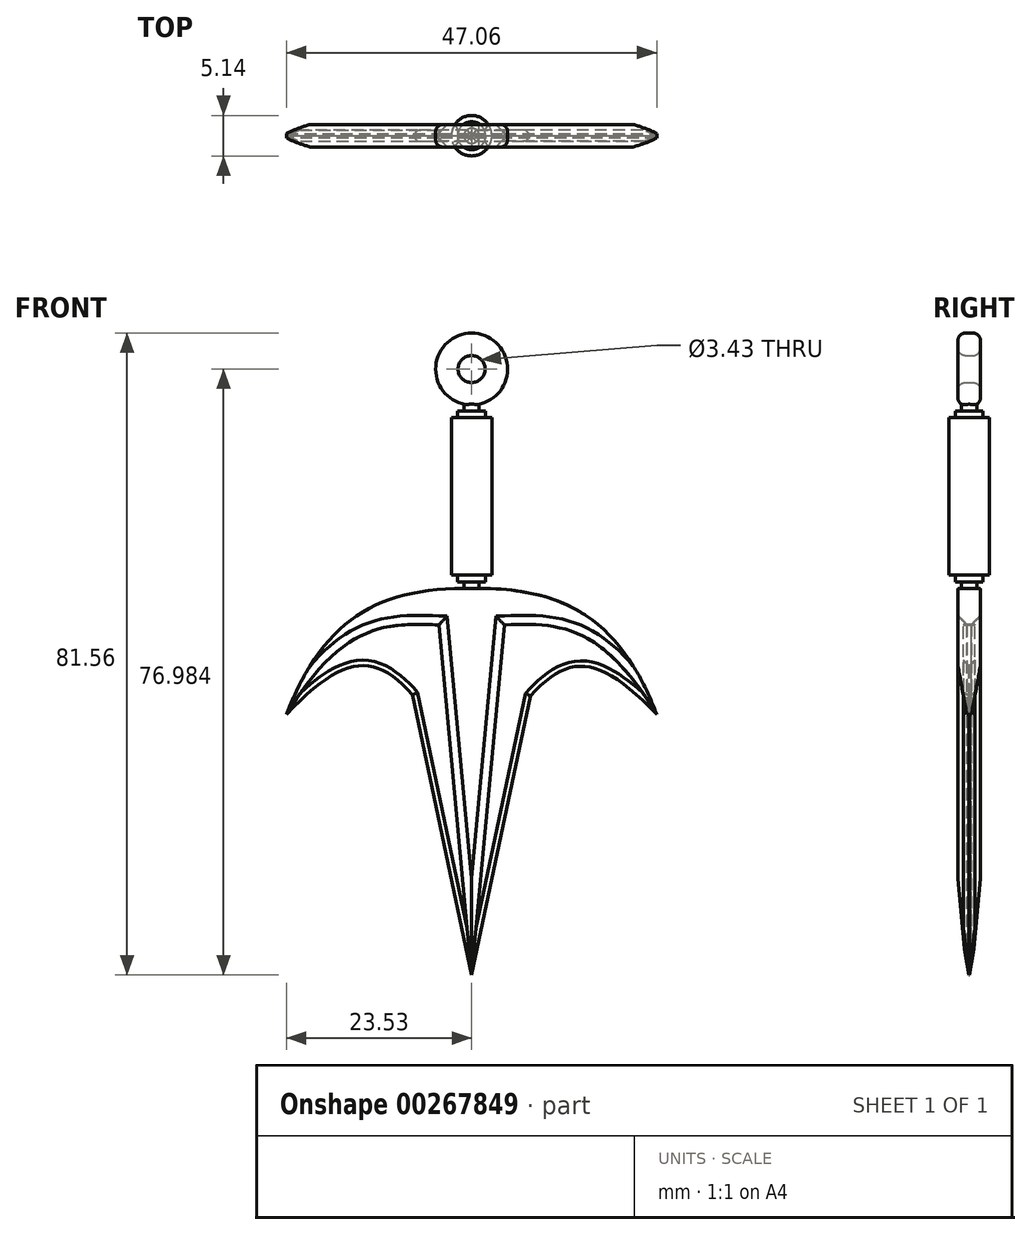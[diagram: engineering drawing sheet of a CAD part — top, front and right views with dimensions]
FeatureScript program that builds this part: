
annotation { "Feature Type Name" : "Feature", "Feature Type Description" : "" }
export const myFeature = defineFeature(function(context is Context, id is Id, definition is map)
    precondition{}
    {
        {
            var Q0;
            Q0=qCreatedBy(makeId("Front.planeOp"),FACE);
            var sketch = newSketch(context, id + "F0", { "sketchPlane" : qUnion([Q0])});
            skLineSegment(sketch, "E0", {"start": v(-2.15, 10.52) * mm, "end": v(2.15, 10.5) * mm});
            skFitSpline(sketch, "E1", {"points": [v(-2.15, 10.52) * mm, v(-52.28, -25.05) * mm], "startDerivative": vector(-77.64, 0.41) * mm, "endDerivative": vector(-28.93, -75.16) * mm});
            skFitSpline(sketch, "E2.MirrorCS", {"points": [v(2.15, 10.52) * mm, v(52.28, -25.05) * mm], "startDerivative": vector(77.64, 0.41) * mm, "endDerivative": vector(28.93, -75.16) * mm});
            skFitSpline(sketch, "E3", {"points": [v(-52.28, -25.05) * mm, v(-16.63, -19.48) * mm], "startDerivative": vector(47.66, 50.06) * mm, "endDerivative": vector(33.37, -37.08) * mm});
            skFitSpline(sketch, "E4.MirrorCS", {"points": [v(52.28, -25.05) * mm, v(16.62, -19.8) * mm], "startDerivative": vector(-47.66, 50.06) * mm, "endDerivative": vector(-33.37, -37.08) * mm});
            skLineSegment(sketch, "E5", {"start": v(-16.63, -19.48) * mm, "end": v(0, -98.6) * mm});
            skLineSegment(sketch, "E6.MirrorCS", {"start": v(16.62, -19.8) * mm, "end": v(0, -98.6) * mm});
            skLineSegment(sketch, "E7", {"start": v(-16.63, -19.48) * mm, "end": v(0, 0) * mm});
            skLineSegment(sketch, "E8.MirrorCS", {"start": v(16.62, -19.8) * mm, "end": v(0, 0) * mm});
            skFitSpline(sketch, "E9", {"points": [v(-52.28, -25.05) * mm, v(0, 0) * mm], "startDerivative": vector(56, 91.77) * mm, "endDerivative": vector(61, 0) * mm});
            skFitSpline(sketch, "E10.MirrorCS", {"points": [v(52.28, -25.05) * mm, v(0, 0) * mm], "startDerivative": vector(-56, 91.77) * mm, "endDerivative": vector(-61, 0) * mm});
            skLineSegment(sketch, "E11", {"start": v(0, -98.6) * mm, "end": v(-8.31, -9.74) * mm});
            skLineSegment(sketch, "E12", {"start": v(0, 10.5) * mm, "end": v(0, -98.6) * mm, "construction": true});
            skLineSegment(sketch, "E13.MirrorCS", {"start": v(0, -98.6) * mm, "end": v(8.31, -9.74) * mm});
            skLineSegment(sketch, "E14", {"start": v(-8.31, -9.74) * mm, "end": v(-9.25, 0.25) * mm});
            skLineSegment(sketch, "E15.MirrorCS", {"start": v(8.31, -9.74) * mm, "end": v(9.25, 0.25) * mm});
            skLineSegment(sketch, "E16", {"start": v(0, 10.5) * mm, "end": v(0, 72.47) * mm, "construction": true});
            skLineSegment(sketch, "E17", {"start": v(2.15, 10.5) * mm, "end": v(2.15, 12.4) * mm});
            skLineSegment(sketch, "E18", {"start": v(2.15, 12.4) * mm, "end": v(3.93, 12.4) * mm});
            skLineSegment(sketch, "E19", {"start": v(3.93, 12.4) * mm, "end": v(3.93, 14.3) * mm});
            skLineSegment(sketch, "E20", {"start": v(3.93, 14.3) * mm, "end": v(5.7, 14.3) * mm});
            skLineSegment(sketch, "E21", {"start": v(5.7, 14.3) * mm, "end": v(5.7, 58.75) * mm});
            skLineSegment(sketch, "E22", {"start": v(5.7, 36.52) * mm, "end": v(-12.22, 36.52) * mm, "construction": true});
            skLineSegment(sketch, "E23.MirrorCS", {"start": v(3.93, 58.74) * mm, "end": v(5.7, 58.75) * mm});
            skLineSegment(sketch, "E24.MirrorCS", {"start": v(2.15, 60.64) * mm, "end": v(3.93, 60.65) * mm});
            skLineSegment(sketch, "E25.MirrorCS", {"start": v(3.93, 60.65) * mm, "end": v(3.93, 58.74) * mm});
            skCircle(sketch, "E26", {"center": v(0, 72.47) * mm, "radius": 10.16 * mm});
            skCircle(sketch, "E27", {"center": v(0, 72.47) * mm, "radius": 3.81 * mm});
            skLineSegment(sketch, "E28", {"start": v(2.14, 62.54) * mm, "end": v(2.15, 60.64) * mm});
            skLineSegment(sketch, "E29", {"start": v(0, 62.31) * mm, "end": v(0, 10.5) * mm});
            skSolve(sketch);
        }
        {
            var Q0;
            Q0=makeQuery(id+"F0.imprint","IMPRINT",FACE,{"disambiguationData":[TD([[makeQuery(id+"F0.imprint","IMPRINT",EDGE,{"derivedFrom":sQuery(id+"F0.wireOp",EDGE,"E27")}),-1.0]])]});
            extrude(context, id + "F1", {"entities" : qUnion([Q0]), "endBound" : BoundingType.SYMMETRIC, "depth" : 6.35 * mm});
        }
        {
            var Q0;
            Q0=makeQuery(id+"F1.opExtrude","CAP_EDGE",EDGE,{"disambiguationData":[OSD([sQuery(id+"F0.wireOp",EDGE,"E26")])],"isStart":false});
            var Q1;
            Q1=makeQuery(id+"F1.opExtrude","CAP_EDGE",EDGE,{"disambiguationData":[OSD([sQuery(id+"F0.wireOp",EDGE,"E26")])],"isStart":true});
            var Q2;
            Q2=makeQuery(id+"F1.opExtrude","CAP_EDGE",EDGE,{"disambiguationData":[OSD([sQuery(id+"F0.wireOp",EDGE,"E27")])],"isStart":true});
            var Q3;
            Q3=makeQuery(id+"F1.opExtrude","CAP_EDGE",EDGE,{"disambiguationData":[OSD([sQuery(id+"F0.wireOp",EDGE,"E27")])],"isStart":false});
            fillet(context, id + "F2", {"entities" : qUnion([Q0, Q1, Q2, Q3]), "radius" : 2.03 * mm, "tangentPropagation" : true, "allowEdgeOverflow" : false});
        }
        {
            var Q0;
            {var subQ2=sQuery(id+"F0.wireOp",EDGE,"E18");Q0=makeQuery(id+"F0.imprint","IMPRINT",FACE,{"disambiguationData":[TD([[makeQuery(id+"F0.imprint","IMPRINT",EDGE,{"derivedFrom":subQ2}),1.0]])]});}
            var Q1;
            Q1=sQuery(id+"F0.wireOp",EDGE,"E29");
            revolve(context, id + "F3", {"operationType" : NewBodyOperationType.ADD, "entities" : qUnion([Q0]), "axis" : qUnion([Q1]), "revolveType" : RevolveType.FULL});
        }
        {
            var Q0;
            {var subQ1=sQuery(id+"F0.wireOp",EDGE,"E1");Q0=makeQuery(id+"F0.imprint","IMPRINT",FACE,{"disambiguationData":[TD([[makeQuery(id+"F0.imprint","IMPRINT",EDGE,{"derivedFrom":subQ1}),1.0]])]});}
            var Q1;
            {var subQ3=sQuery(id+"F0.wireOp",EDGE,"E11");Q1=makeQuery(id+"F0.imprint","IMPRINT",FACE,{"disambiguationData":[TD([[makeQuery(id+"F0.imprint","IMPRINT",EDGE,{"derivedFrom":subQ3}),-1.0]])]});}
            var Q2;
            {var subQ3=sQuery(id+"F0.wireOp",EDGE,"E14");Q2=makeQuery(id+"F0.imprint","IMPRINT",FACE,{"disambiguationData":[TD([[makeQuery(id+"F0.imprint","IMPRINT",EDGE,{"derivedFrom":subQ3}),-1.0]])]});}
            var Q3;
            {var subQ5=sQuery(id+"F0.wireOp",EDGE,"E15.MirrorCS");Q3=makeQuery(id+"F0.imprint","IMPRINT",FACE,{"disambiguationData":[TD([[makeQuery(id+"F0.imprint","IMPRINT",EDGE,{"derivedFrom":subQ5}),1.0]])]});}
            extrude(context, id + "F4", {"entities" : qUnion([Q0, Q1, Q2, Q3]), "endBound" : BoundingType.SYMMETRIC, "depth" : 6.35 * mm});
        }
        {
            var Q0;
            {var subQ0=sQuery(id+"F0.wireOp",EDGE,"E3");Q0=makeQuery(id+"F0.imprint","IMPRINT",FACE,{"disambiguationData":[TD([[makeQuery(id+"F0.imprint","IMPRINT",EDGE,{"derivedFrom":subQ0}),1.0]])]});}
            var Q1;
            {var subQ0=sQuery(id+"F0.wireOp",EDGE,"E5");Q1=makeQuery(id+"F0.imprint","IMPRINT",FACE,{"disambiguationData":[TD([[makeQuery(id+"F0.imprint","IMPRINT",EDGE,{"derivedFrom":subQ0}),1.0]])]});}
            var Q2;
            {var subQ0=sQuery(id+"F0.wireOp",EDGE,"E4.MirrorCS");Q2=makeQuery(id+"F0.imprint","IMPRINT",FACE,{"disambiguationData":[TD([[makeQuery(id+"F0.imprint","IMPRINT",EDGE,{"derivedFrom":subQ0}),-1.0]])]});}
            var Q3;
            {var subQ0=sQuery(id+"F0.wireOp",EDGE,"E6.MirrorCS");Q3=makeQuery(id+"F0.imprint","IMPRINT",FACE,{"disambiguationData":[TD([[makeQuery(id+"F0.imprint","IMPRINT",EDGE,{"derivedFrom":subQ0}),-1.0]])]});}
            extrude(context, id + "F5", {"entities" : qUnion([Q0, Q1, Q2, Q3]), "endBound" : BoundingType.SYMMETRIC, "depth" : 3.17 * mm});
        }
        {
            var Q0;
            Q0=makeQuery(id+"F5.opExtrude","CAP_EDGE",EDGE,{"disambiguationData":[OSD([sQuery(id+"F0.wireOp",EDGE,"E5")])],"isStart":false});
            var Q1;
            Q1=makeQuery(id+"F5.opExtrude","CAP_EDGE",EDGE,{"disambiguationData":[OSD([sQuery(id+"F0.wireOp",EDGE,"E3")])],"isStart":false});
            var Q2;
            Q2=makeQuery(id+"F5.opExtrude","CAP_EDGE",EDGE,{"disambiguationData":[OSD([sQuery(id+"F0.wireOp",EDGE,"E5")])],"isStart":true});
            var Q3;
            Q3=makeQuery(id+"F5.opExtrude","CAP_EDGE",EDGE,{"disambiguationData":[OSD([sQuery(id+"F0.wireOp",EDGE,"E3")])],"isStart":true});
            chamfer(context, id + "F6", {"entities" : qUnion([Q0, Q1, Q2, Q3]), "width" : 1.52 * mm, "tangentPropagation" : true});
        }
        {
            var Q0;
            Q0=makeQuery(id+"F5.opExtrude","CAP_EDGE",EDGE,{"disambiguationData":[OSD([sQuery(id+"F0.wireOp",EDGE,"E6.MirrorCS")])],"isStart":false});
            var Q1;
            Q1=makeQuery(id+"F5.opExtrude","CAP_EDGE",EDGE,{"disambiguationData":[OSD([sQuery(id+"F0.wireOp",EDGE,"E4.MirrorCS")])],"isStart":false});
            var Q2;
            Q2=makeQuery(id+"F5.opExtrude","CAP_EDGE",EDGE,{"disambiguationData":[OSD([sQuery(id+"F0.wireOp",EDGE,"E4.MirrorCS")])],"isStart":true});
            var Q3;
            Q3=makeQuery(id+"F5.opExtrude","CAP_EDGE",EDGE,{"disambiguationData":[OSD([sQuery(id+"F0.wireOp",EDGE,"E6.MirrorCS")])],"isStart":true});
            chamfer(context, id + "F7", {"entities" : qUnion([Q0, Q1, Q2, Q3]), "width" : 1.52 * mm, "tangentPropagation" : true});
        }
        {
            var Q0;
            Q0=makeQuery(id+"F4.opExtrude","CAP_EDGE",EDGE,{"disambiguationData":[OSD([sQuery(id+"F0.wireOp",EDGE,"E7")])],"isStart":false});
            var Q1;
            Q1=makeQuery(id+"F4.opExtrude","CAP_EDGE",EDGE,{"disambiguationData":[OSD([sQuery(id+"F0.wireOp",EDGE,"E11")])],"isStart":false});
            var Q2;
            Q2=makeQuery(id+"F4.opExtrude","CAP_EDGE",EDGE,{"disambiguationData":[OSD([sQuery(id+"F0.wireOp",EDGE,"d41bfb26-c881-4ffa-98e3-99cad1ed0fc00.MirrorCS")])],"isStart":false});
            var Q3;
            Q3=makeQuery(id+"F4.opExtrude","CAP_EDGE",EDGE,{"disambiguationData":[OSD([sQuery(id+"F0.wireOp",EDGE,"E8.MirrorCS")])],"isStart":false});
            var Q4;
            Q4=makeQuery(id+"F4.opExtrude","CAP_EDGE",EDGE,{"disambiguationData":[OSD([sQuery(id+"F0.wireOp",EDGE,"E7")])],"isStart":true});
            var Q5;
            Q5=makeQuery(id+"F4.opExtrude","CAP_EDGE",EDGE,{"disambiguationData":[OSD([sQuery(id+"F0.wireOp",EDGE,"E8.MirrorCS")])],"isStart":true});
            var Q6;
            Q6=makeQuery(id+"F4.opExtrude","CAP_EDGE",EDGE,{"disambiguationData":[OSD([sQuery(id+"F0.wireOp",EDGE,"d41bfb26-c881-4ffa-98e3-99cad1ed0fc00.MirrorCS")])],"isStart":true});
            var Q7;
            Q7=makeQuery(id+"F4.opExtrude","CAP_EDGE",EDGE,{"disambiguationData":[OSD([sQuery(id+"F0.wireOp",EDGE,"E11")])],"isStart":true});
            var Q8;
            Q8=makeQuery(id+"F4.opExtrude","CAP_EDGE",EDGE,{"disambiguationData":[OSD([sQuery(id+"F0.wireOp",EDGE,"E13.MirrorCS")])],"isStart":true});
            var Q9;
            Q9=makeQuery(id+"F4.opExtrude","CAP_EDGE",EDGE,{"disambiguationData":[OSD([sQuery(id+"F0.wireOp",EDGE,"E13.MirrorCS")])],"isStart":false});
            chamfer(context, id + "F8", {"entities" : qUnion([Q0, Q1, Q2, Q3, Q4, Q5, Q6, Q7, Q8, Q9]), "width" : 2.54 * mm, "tangentPropagation" : true});
        }
        {
            var Q0;
            Q0=qCreatedBy(makeId("Right.planeOp"),FACE);
            var sketch = newSketch(context, id + "F9", { "sketchPlane" : qUnion([Q0])});
            skLineSegment(sketch, "E30", {"start": v(0, -99.02) * mm, "end": v(-21.64, -99.02) * mm});
            skLineSegment(sketch, "E31", {"start": v(-21.64, -99.02) * mm, "end": v(-7.44, -55.2) * mm});
            skLineSegment(sketch, "E32", {"start": v(0, -99.02) * mm, "end": v(0, -42.48) * mm, "construction": true});
            skLineSegment(sketch, "E33.MirrorCS", {"start": v(21.64, -99.02) * mm, "end": v(7.44, -55.2) * mm});
            skLineSegment(sketch, "E34.MirrorCS", {"start": v(0, -99.02) * mm, "end": v(21.64, -99.02) * mm});
            skLineSegment(sketch, "E35.MirrorCS", {"start": v(0, -99.02) * mm, "end": v(1, -75.67) * mm});
            skPoint(sketch, "E36.endSnap0", {"position": v(-10.82, -99.02) * mm});
            skLineSegment(sketch, "E37", {"start": v(7.44, -55.2) * mm, "end": v(0, -99.02) * mm});
            skLineSegment(sketch, "E38", {"start": v(-7.44, -55.2) * mm, "end": v(0, -99.02) * mm});
            skSolve(sketch);
        }
        {
            var Q0;
            Q0 = qSketchRegion(id + "F9", true);
            extrude(context, id + "F10", {"entities" : qUnion([Q0]), "operationType" : NewBodyOperationType.REMOVE, "endBound" : BoundingType.SYMMETRIC, "oppositeDirection" : true, "depth" : 25.4 * mm});
        }
        {
            var Q0;
            Q0=makeQuery(id+"F4.opExtrude","CAP_EDGE",EDGE,{"disambiguationData":[OSD([sQuery(id+"F0.wireOp",EDGE,"E10.MirrorCS")])],"isStart":true});
            var Q1;
            Q1=makeQuery(id+"F4.opExtrude","CAP_EDGE",EDGE,{"disambiguationData":[OSD([sQuery(id+"F0.wireOp",EDGE,"E9")])],"isStart":true});
            var Q2;
            Q2=makeQuery(id+"F4.opExtrude","CAP_EDGE",EDGE,{"disambiguationData":[OSD([sQuery(id+"F0.wireOp",EDGE,"E10.MirrorCS")])],"isStart":false});
            var Q3;
            Q3=makeQuery(id+"F4.opExtrude","CAP_EDGE",EDGE,{"disambiguationData":[OSD([sQuery(id+"F0.wireOp",EDGE,"E9")])],"isStart":false});
            chamfer(context, id + "F11", {"entities" : qUnion([Q0, Q1, Q2, Q3]), "width" : 2.54 * mm, "tangentPropagation" : true});
        }
        {
            var Q0;
            Q0=makeQuery(id+"F1.opExtrude","SWEPT_BODY",BODY,{"disambiguationData":[OSD([sQuery(id+"F0.wireOp",EDGE,"E26"),sQuery(id+"F0.wireOp",EDGE,"E27")])]});
            var Q1;
            Q1=makeQuery(id+"F4.opExtrude","SWEPT_BODY",BODY,{"disambiguationData":[OSD([sQuery(id+"F0.wireOp",EDGE,"E0"),sQuery(id+"F0.wireOp",EDGE,"E1"),sQuery(id+"F0.wireOp",EDGE,"E2.MirrorCS"),sQuery(id+"F0.wireOp",EDGE,"E9"),sQuery(id+"F0.wireOp",EDGE,"E10.MirrorCS"),sQuery(id+"F0.wireOp",EDGE,"E11"),sQuery(id+"F0.wireOp",EDGE,"E13.MirrorCS"),sQuery(id+"F0.wireOp",EDGE,"E14"),sQuery(id+"F0.wireOp",EDGE,"E15.MirrorCS"),sQuery(id+"F0.wireOp",EDGE,"E17")])]});
            var Q2;
            Q2=makeQuery(id+"F5.opExtrude","SWEPT_BODY",BODY,{"disambiguationData":[OSD([sQuery(id+"F0.wireOp",EDGE,"E3"),sQuery(id+"F0.wireOp",EDGE,"E5"),sQuery(id+"F0.wireOp",EDGE,"E9"),sQuery(id+"F0.wireOp",EDGE,"E11"),sQuery(id+"F0.wireOp",EDGE,"E14")])]});
            var Q3;
            Q3=makeQuery(id+"F5.opExtrude","SWEPT_BODY",BODY,{"disambiguationData":[OSD([sQuery(id+"F0.wireOp",EDGE,"E4.MirrorCS"),sQuery(id+"F0.wireOp",EDGE,"E6.MirrorCS"),sQuery(id+"F0.wireOp",EDGE,"E10.MirrorCS"),sQuery(id+"F0.wireOp",EDGE,"E13.MirrorCS"),sQuery(id+"F0.wireOp",EDGE,"E15.MirrorCS")])]});
            var Q4;
            Q4=qCreatedBy(makeId("Origin.pointOp"),VERTEX);
            transform(context, id + "F12", {"entities" : qUnion([Q0, Q1, Q2, Q3]), "transformType" : TransformType.SCALE_UNIFORMLY, "scale" : .45, "scalePoint" : qUnion([Q4]), "makeCopy" : false});
        }
    });
